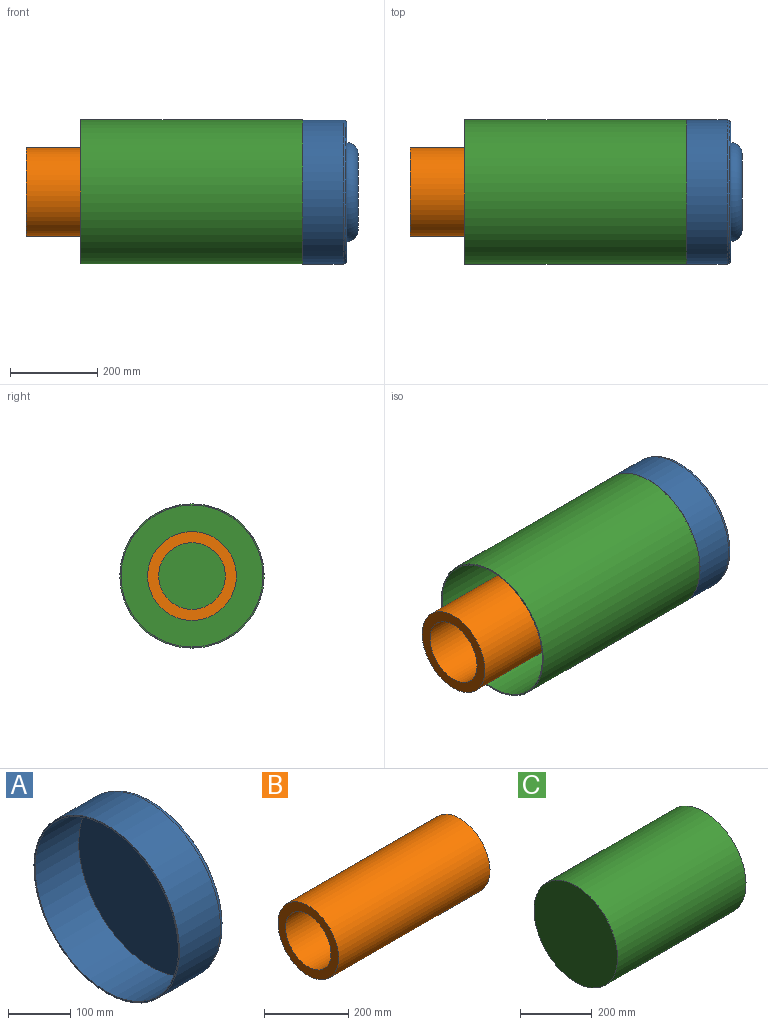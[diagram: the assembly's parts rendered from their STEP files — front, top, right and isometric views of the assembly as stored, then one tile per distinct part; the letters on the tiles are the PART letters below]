
ASSEMBLY  parts=3 mates=2
PART A: 8 faces, bbox 127x357.4x357.4 mm
  f0: cylinder r=165.1mm len=330.2mm, axis (-1,0,0), area 96436.6mm2, adj f2,f5
  f1: plane 312.93x312.93mm, normal (1,0,0), area 36467.7mm2, adj f5,f7
  f2: plane 330.2x330.2mm, normal (-1,0,0), area 2614.6mm2, adj f0,f3
  f3: cylinder r=162.56mm len=325.12mm, axis (-1,0,0), area 101179.3mm2, adj f2,f4
  f4: plane 325.12x325.12mm, normal (-1,0,0), area 83019mm2, adj f3
  f5: torus R=156.46mm, axis (1,0,0), area 13804.6mm2, adj f0,f1
  f6: plane 176.12x176.12mm, normal (1,0,0), area 24361.2mm2, adj f7
  f7: torus R=88.06mm, axis (1,0,0), area 26129mm2, adj f1,f6
PART B: 4 faces, bbox 508x203.2x203.2 mm
  f0: cylinder r=101.6mm len=508mm, axis (-1,0,0), area 324292.8mm2, adj f1,f2
  f1: plane 203.2x203.2mm, normal (1,0,0), area 14187.8mm2, adj f0,f3
  f2: plane 203.2x203.2mm, normal (-1,0,0), area 14187.8mm2, adj f0,f3
  f3: cylinder r=76.2mm len=508mm, axis (-1,0,0), area 243219.6mm2, adj f1,f2
PART C: 5 faces, bbox 508x330.2x330.2 mm
  f0: cylinder r=165.1mm len=508mm, axis (-1,0,0), area 526975.8mm2, adj f1,f2
  f1: plane 330.2x330.2mm, normal (1,0,0), area 2614.6mm2, adj f0,f3
  f2: plane 330.2x330.2mm, normal (-1,0,0), area 85633.6mm2, adj f0
  f3: cylinder r=162.56mm len=505.46mm, axis (-1,0,0), area 516274.1mm2, adj f1,f4
  f4: plane 325.12x325.12mm, normal (1,0,0), area 83019mm2, adj f3
PLACE A t=(689.07,168.06,-142.72)mm
PLACE B t=(55.85,168.06,-142.72)mm
PLACE C rot(axis=(0,1,0),180deg) t=(689.07,168.06,-142.72)mm
MATE cylindrical B.f0 <-> C.f0  axis (1,0,0) through (563.85,168.06,-142.72)mm
MATE revolute A.f0 <-> C.f0  axis (-1,0,0) through (689.07,168.06,-142.72)mm
